# Revit family: Hager-Orion_Plus-IP65-D300-Cl.II-Poly_double_encl-630A-FR-fr
name_source: partatom
category: Electrical Equipment
units: mm (PartAtom-declared; Revit-internal decimal feet)

## family parameters
Cut with Voids When Loaded = No
Host = Face
Panel Configuration = Two Columns, Circuits Across
Part Type = Panelboard
Room Calculation Point = No
Round Connector Dimension = Use Diameter
Shared = No

## types (3) — shared parameters
EF000003 - mode de pose = EV012274 - installation au sol
EF000007 - couleur = EV000270 - gris
EF000049 - profondeur = 300 mm  [stored 0.984252 ft]
EF000116 - numéro RAL = 7035
EF000118 - avec cadre/support de montage = Yes
EF000339 - type de capot = EV001012 - couvercle
EF001088 - possibilité de montage en saillie = No
EF001131 - profondeur intérieure = 300 mm  [stored 0.984252 ft]
EF001596 - matériau du boîtier/corps = EV000139 - plastique
EF001613 - maintien de fonction = EV000494 - sans
EF003532 - convient pour utilisation à l’extérieur = No
EF004293 - indice de protection contre les chocs (IK) = EV006814 - IK08
EF004464 - type de porte = EV002646 - unique
EF005474 - indice de protection (IP) = EV006421 - IP65
EF006244 - couvercle/porte transparent(e) = No
EF006306 - avec serrure = Yes
EF007800 - adapté à un parafoudre = No
EF008873 - courant nominal (In) = 630 A
EF009170 - épaisseur de matériau du boîtier = 2 mm  [stored 0.00656168 ft]
EF009171 - épaisseur de matériau de la porte/du couvercle = 2 mm  [stored 0.00656168 ft]
EF009212 - finition du couvercle = EV000116 - fermé
EF015940 - couvercle avec décharge de pression = No
HG000002 - avec porte = Yes
HG000003 - Gamme = Orion Plus
HG000006 - Encastré = No
HG000010 - Portes asymétriques = No
HG000023 - Armoire double section = Yes
HG000024 - Hauteur de la section basse = 800 mm  [stored 2.62467 ft]
HG000026 - Installation au sol = Yes
HG000027 - Hauteur du socle = 70 mm  [stored 0.229659 ft]
Manufacturer = Hager
Type Comments = Orion Plus
zero-valued in all types: Default Elevation, EF000218 - profondeur d'encastrement, EF000437 - nombre d'entrées de conduit, EF002950 - largeur en nombre de modules, EF009554 - nombre d'ouvertures pour plaques à bride

## per-type parameters (varying)
| type | EF000008 - largeur | EF000040 - hauteur | EF000266 - nombre de rangées | EF004427 - nombre de modules | HG000004 - Référence fabricant | HG000009 - Porte à double battant |
| installation au sol IP65 L1100 H2050 P300  - FL368B | 1100 mm | 2050 mm  [stored 6.72572 ft] | 5 | 230 | FL368B | Yes |
| installation au sol IP65 L850 H1450 P300  - FL352B | 850 mm  [stored 2.78871 ft] | 1450 mm | 3 | 111 | FL352B | No |
| installation au sol IP65 L850 H1750 P300  - FL354B | 850 mm  [stored 2.78871 ft] | 1750 mm  [stored 5.74147 ft] | 3 | 111 | FL354B | No |

note: [stored X ft] marks values corroborated as IEEE doubles in the binary element streams (Revit-internal decimal feet)

## geometry (parser evidence)
native form markers: Sweep x10
no freeform markers — native parametric forms only
